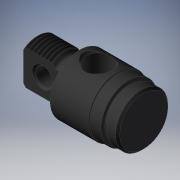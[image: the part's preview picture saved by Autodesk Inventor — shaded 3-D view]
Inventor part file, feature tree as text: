
AUTODESK INVENTOR PART (.ipt)
format: ipt  version: 2019 (Build 230136000, 136)  size: 276,992 bytes
history: native  units: mm
features: other x126, sketch x7, revolve x6, thread x1, extrude x1
ambient origin geometry x8: Origin, YZ Plane, XZ Plane, XY Plane, X Axis, Y Axis, Z Axis, Center Point
bodies: Solid1 (feature_tree)
feature tree (141):
  revolve  "Revolution1"  Angle=360.0deg
  revolve  "Revolution2"  Angle=360.0deg
  thread  "Thread1"  [1 undecoded]
  revolve  "Revolution3"  [1 undecoded]
  revolve  "Revolution4"  [1 undecoded]
  revolve  "Revolution5"  [1 undecoded]
  extrude  "Extrusion1"  [1 undecoded]
  revolve  "Revolution6"  [1 undecoded]
  other  "b1_XY"
  other  "b1_YZ"
  other  "b1_ZX"
  other  "b1_X"
  other  "b1_Y"
  other  "b1_Z"
  other  "b1_Center"
  other  "b2_XY"
  other  "b2_YZ"
  other  "b2_ZX"
  other  "b2_X"
  other  "b2_Y"
  other  "b2_Z"
  other  "b2_Center"
  other  "cl1_XY"
  other  "cl1_YZ"
  other  "cl1_ZX"
  other  "cl1_X"
  other  "cl1_Y"
  other  "cl1_Z"
  other  "cl1_Center"
  other  "cl2_XY"
  other  "cl2_YZ"
  other  "cl2_ZX"
  other  "cl2_X"
  other  "cl2_Y"
  other  "cl2_Z"
  other  "cl2_Center"
  other  "ecut1_XY"
  other  "ecut1_YZ"
  other  "ecut1_ZX"
  other  "ecut1_X"
  other  "ecut1_Y"
  other  "ecut1_Z"
  other  "ecut1_Center"
  other  "ecut2_XY"
  other  "ecut2_YZ"
  other  "ecut2_ZX"
  other  "ecut2_X"
  other  "ecut2_Y"
  other  "ecut2_Z"
  other  "ecut2_Center"
  other  "ee_XY"
  other  "ee_YZ"
  other  "ee_ZX"
  other  "ee_X"
  other  "ee_Y"
  other  "ee_Z"
  other  "ee_Center"
  other  "od1_XY"
  other  "od1_YZ"
  other  "od1_ZX"
  other  "od1_X"
  other  "od1_Y"
  other  "od1_Z"
  other  "od1_Center"
  other  "od2_XY"
  other  "od2_YZ"
  other  "od2_ZX"
  other  "od2_X"
  other  "od2_Y"
  other  "od2_Z"
  other  "od2_Center"
  other  "od3_XY"
  other  "od3_YZ"
  other  "od3_ZX"
  other  "od3_X"
  other  "od3_Y"
  other  "od3_Z"
  other  "od3_Center"
  other  "od4_XY"
  other  "od4_YZ"
  other  "od4_ZX"
  other  "od4_X"
  other  "od4_Y"
  other  "od4_Z"
  other  "od4_Center"
  other  "to_body_XY"
  other  "to_body_YZ"
  other  "to_body_ZX"
  other  "to_body_X"
  other  "to_body_Y"
  other  "to_body_Z"
  other  "to_body_Center"
  other  "to_dummy_XY"
  other  "to_dummy_YZ"
  other  "to_dummy_ZX"
  other  "to_dummy_X"
  other  "to_dummy_Y"
  other  "to_dummy_Z"
  other  "to_dummy_Center"
  other  "to_nut_XY"
  other  "to_nut_YZ"
  other  "to_nut_ZX"
  other  "to_nut_X"
  other  "to_nut_Y"
  other  "to_nut_Z"
  other  "to_nut_Center"
  other  "to_pin_XY"
  other  "to_pin_YZ"
  other  "to_pin_ZX"
  other  "to_pin_X"
  other  "to_pin_Y"
  other  "to_pin_Z"
  other  "to_pin_Center"
  other  "to_stroke_adjuster_XY"
  other  "to_stroke_adjuster_YZ"
  other  "to_stroke_adjuster_ZX"
  other  "to_stroke_adjuster_X"
  other  "to_stroke_adjuster_Y"
  other  "to_stroke_adjuster_Z"
  other  "to_stroke_adjuster_Center"
  other  "z1_XY"
  other  "z1_YZ"
  other  "z1_ZX"
  other  "z1_X"
  other  "z1_Y"
  other  "z1_Z"
  other  "z1_Center"
  other  "z2_XY"
  other  "z2_YZ"
  other  "z2_ZX"
  other  "z2_X"
  other  "z2_Y"
  other  "z2_Z"
  other  "z2_Center"
  sketch  "Sketch_1"  dims[d0=360.0deg d1=360.0deg]
  sketch  "Sketch_2"  dims[d2=9.87933mm d3=0.0mm d4=360.0deg d5=360.0deg]
  sketch  "Sketch_6"  dims[d6=360.0deg d7=15.9766mm d8=0.0mm]
  sketch  "Sketch_8"  dims[d9=360.0deg]
  sketch  "Sketch_29"  dims[d10=0.0mm d11=0.0mm d12=0.0mm d13=0.0mm d14=0.0mm d15=0.0mm d16=0.0mm d17=0.0mm d18=0.0mm d19=0.0mm d20=0.0mm d21=0.0mm]
  sketch  "Sketch_38"
  sketch  "Sketch_36"
note: 6 required parameter values undecoded (feature->parameter linkage not recoverable at this tier; creation-order binding heuristic only, values carry confidence <= 0.55)